# Revit family: Faucet-Lavatory-Grohe-Essence-20431_Series
name_source: partatom
category: Plumbing Fixtures
revit_build: Autodesk Revit 2014 (Build: 20130308_1515(x64)
units: mm (PartAtom-declared; Revit-internal decimal feet)

## types (3) — shared parameters
ADA Compliant = Yes
Assembly Code = D2020300
CW Connection = Yes
CWFU = 1.5
CalGreen Compliant = Yes
Cold Water Connection Diameter = 3/8"
Default Elevation = 0"
Description = Essence 8'' Widespread Two-Handle Bathroom Faucet L-Size
HW Connection = Yes
HWFU = 1.5
Height = 9 5/8"
Hot Water Connection Diameter = 0"
Installation Type = Deck-Mounted
Length = 4 1/2"
Manufacturer = Grohe
Price = Prices may vary. Please consult Manufacturer Representative for most up-to-date price list.
Product Page URL = https://www.grohe.us
URL = https://www.grohe.us
Vent Connection = No
Warranty Documentation Link = https://cdn.cloud.grohe.com
Waste Connection = No
Width = 8"
cUPC Compliant = Yes
zero-valued in all types: WFU

## per-type parameters (varying)
| type | Finish | Flow Rate | Material |
| 20431A0A | Metal-Grohe-A0A-Hard Graphite | 1.5 gpm (5.7 L/min) | Metal-Grohe-A0A-Hard Graphite |
| 20431BEA | Metal-Grohe-BEA-Polished Nickel | 1.2 gpm (4.56 L/min) | Metal-Grohe-BEA-Polished Nickel |
| 20431GNA | Metal-Grohe-GNA-Brushed Cool Sunset | 1.2 gpm (4.56 L/min) | Metal-Grohe-GNA-Brushed Cool Sunset |

note: column(s) folded — value = type name in every type: Model

## geometry (parser evidence)
native form markers: Sweep x1
no freeform markers — native parametric forms only
